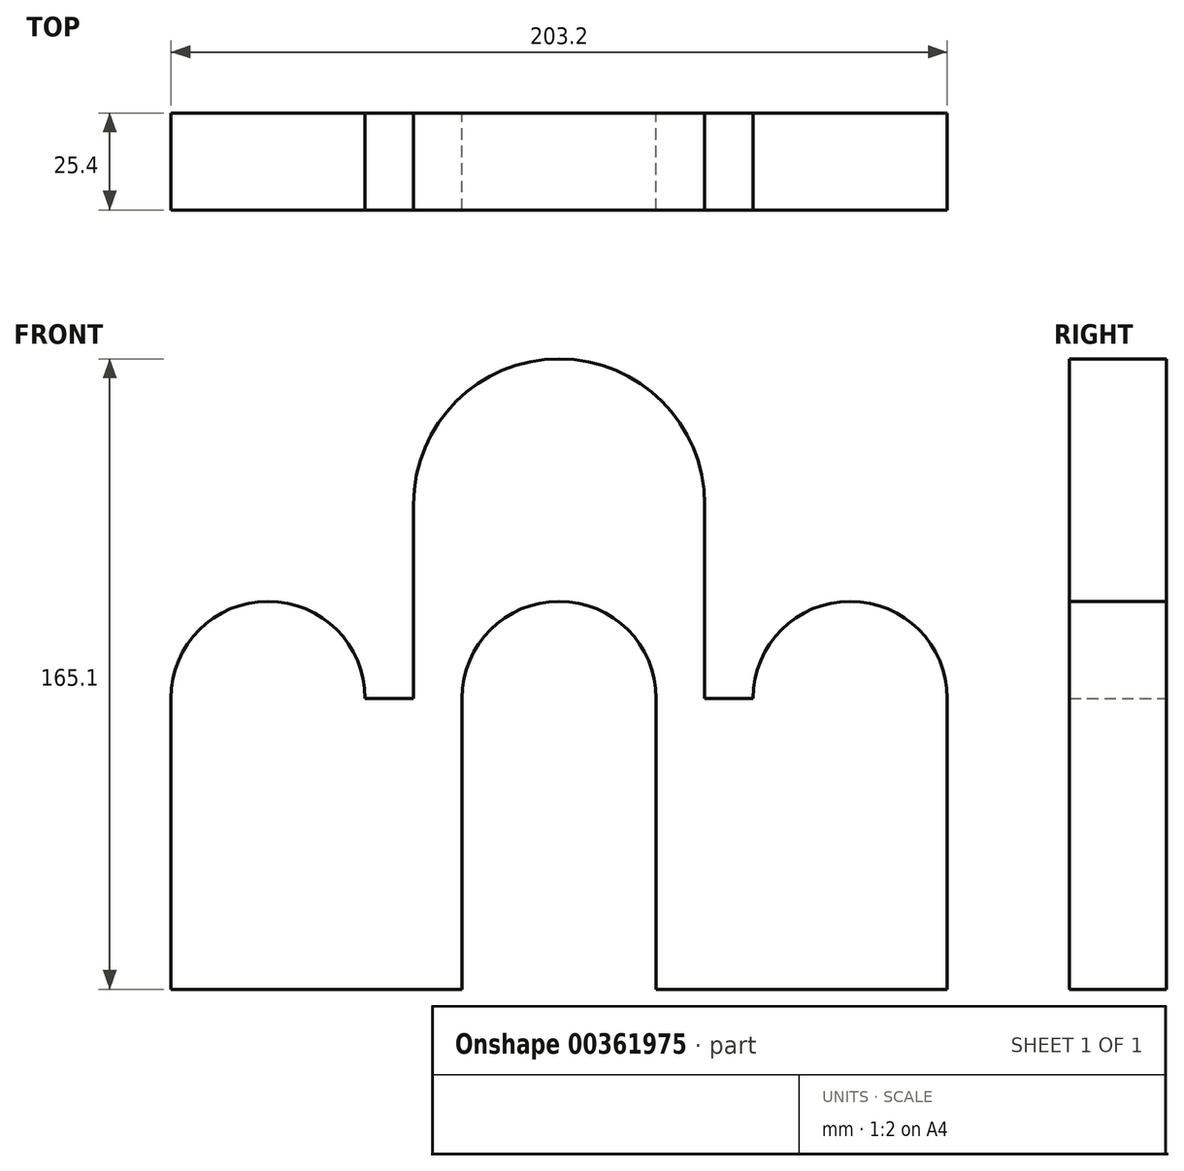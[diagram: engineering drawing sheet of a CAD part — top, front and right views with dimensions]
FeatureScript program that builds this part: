
annotation { "Feature Type Name" : "Feature", "Feature Type Description" : "" }
export const myFeature = defineFeature(function(context is Context, id is Id, definition is map)
    precondition{}
    {
        {
            var Q0;
            Q0=qCreatedBy(makeId("Front.planeOp"),FACE);
            var sketch = newSketch(context, id + "F0", { "sketchPlane" : qUnion([Q0])});
            skLineSegment(sketch, "E0", {"start": v(0, 0) * mm, "end": v(76.2, 0) * mm});
            skLineSegment(sketch, "E1", {"start": v(0, 0) * mm, "end": v(0, 76.2) * mm});
            skLineSegment(sketch, "E2", {"start": v(76.2, 0) * mm, "end": v(76.2, 76.2) * mm});
            skArc(sketch, "E3", {"start": v(0, 76.2) * mm, "mid": v(25.4, 101.6) * mm, "end": v(50.8, 76.2) * mm});
            skLineSegment(sketch, "E4", {"start": v(0, 76.2) * mm, "end": v(50.8, 76.2) * mm, "construction": true});
            skArc(sketch, "E5", {"start": v(76.2, 76.2) * mm, "mid": v(83.64, 94.16) * mm, "end": v(101.6, 101.6) * mm});
            skLineSegment(sketch, "E6", {"start": v(101.6, 76.2) * mm, "end": v(101.6, 101.6) * mm, "construction": true});
            skLineSegment(sketch, "E7", {"start": v(50.8, 76.2) * mm, "end": v(63.5, 76.2) * mm});
            skLineSegment(sketch, "E8", {"start": v(63.5, 76.2) * mm, "end": v(63.5, 127) * mm});
            skArc(sketch, "E9", {"start": v(63.5, 127) * mm, "mid": v(74.66, 153.94) * mm, "end": v(101.6, 165.1) * mm});
            skArc(sketch, "E10.MirrorCS", {"start": v(139.7, 127) * mm, "mid": v(128.54, 153.94) * mm, "end": v(101.6, 165.1) * mm});
            skLineSegment(sketch, "E11.MirrorCS", {"start": v(139.7, 76.2) * mm, "end": v(139.7, 127) * mm});
            skLineSegment(sketch, "E12.MirrorCS", {"start": v(152.4, 76.2) * mm, "end": v(139.7, 76.2) * mm});
            skArc(sketch, "E13.MirrorCS", {"start": v(203.2, 76.2) * mm, "mid": v(177.8, 101.6) * mm, "end": v(152.4, 76.2) * mm});
            skLineSegment(sketch, "E14.MirrorCS", {"start": v(203.2, 0) * mm, "end": v(203.2, 76.2) * mm});
            skLineSegment(sketch, "E15.MirrorCS", {"start": v(203.2, 0) * mm, "end": v(127, 0) * mm});
            skLineSegment(sketch, "E16.MirrorCS", {"start": v(127, 0) * mm, "end": v(127, 76.2) * mm});
            skArc(sketch, "E17.MirrorCS", {"start": v(127, 76.2) * mm, "mid": v(119.56, 94.16) * mm, "end": v(101.6, 101.6) * mm});
            skSolve(sketch);
        }
        {
            var Q0;
            Q0 = qSketchRegion(id + "F0", true);
            extrude(context, id + "F1", {"entities" : qUnion([Q0]), "depth" : 25.4 * mm});
        }
    });
